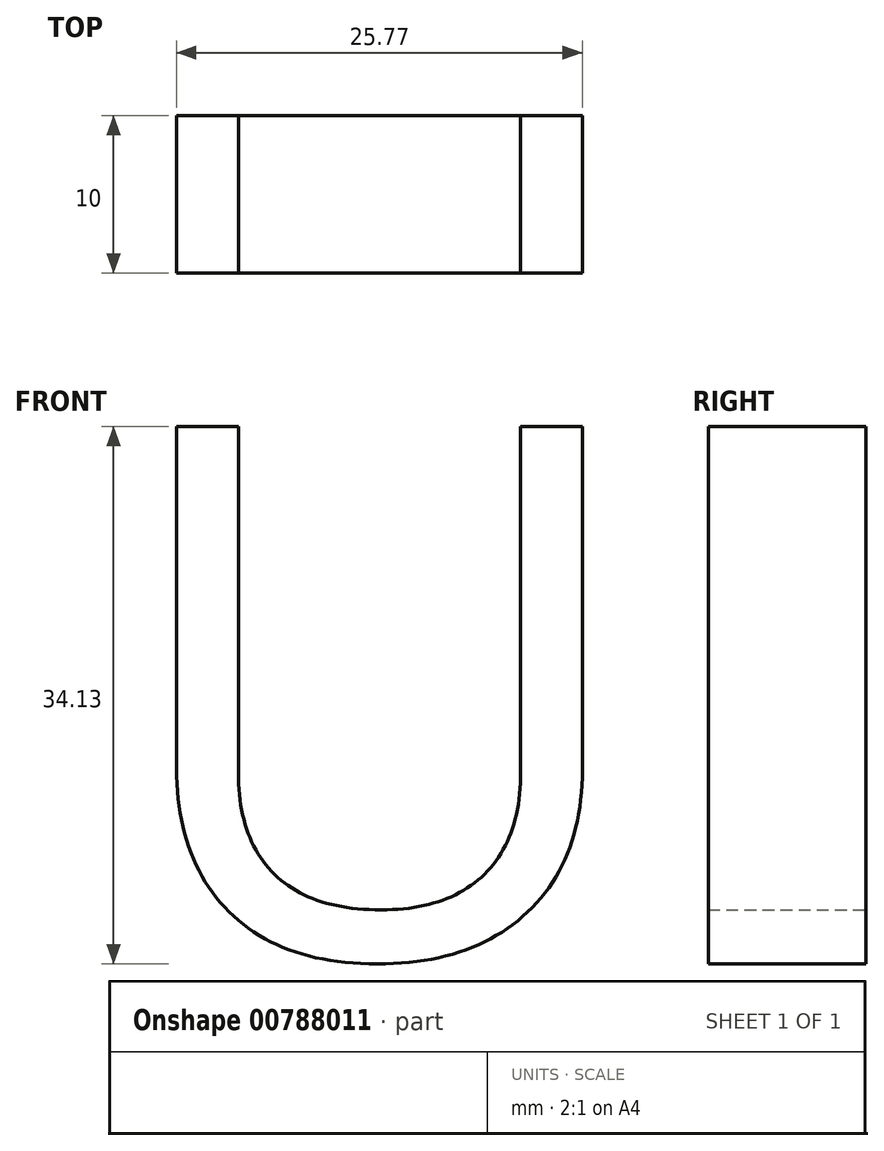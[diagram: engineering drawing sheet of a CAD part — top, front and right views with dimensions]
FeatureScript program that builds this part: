
annotation { "Feature Type Name" : "Feature", "Feature Type Description" : "" }
export const myFeature = defineFeature(function(context is Context, id is Id, definition is map)
    precondition{}
    {
        {
            var Q0;
            Q0=qCreatedBy(makeId("Front.planeOp"),FACE);
            var sketch = newSketch(context, id + "F0", { "sketchPlane" : qUnion([Q0])});
            skText(sketch, "E0", { "text": "U", "fontName": "OpenSans-Regular.ttf"});
            const initialGuessF0  = {"E0": [-0.03312, 0, 1, 0, 0.03396]};
            skSetInitialGuess(sketch, initialGuessF0);
            skSolve(sketch);
        }
        {
            var Q0;
            Q0 = qSketchRegion(id + "F0", true);
            extrude(context, id + "F1", {"entities" : qUnion([Q0]), "depth" : 10 * mm, "offsetDistance" : 25.4 * mm});
        }
    });
